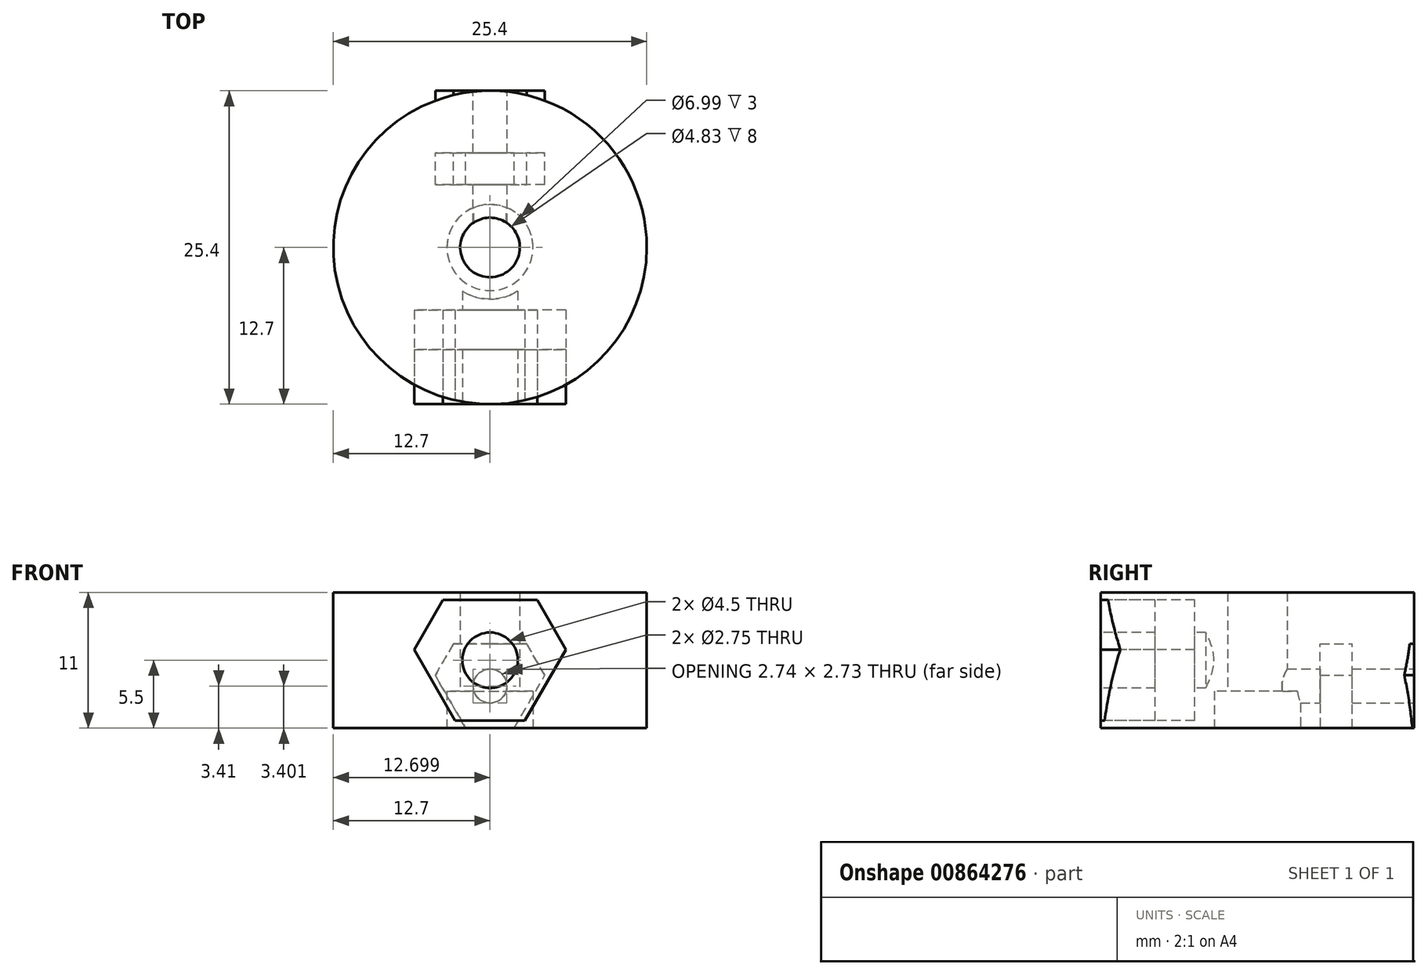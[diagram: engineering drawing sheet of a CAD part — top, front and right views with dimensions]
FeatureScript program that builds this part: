
annotation { "Feature Type Name" : "Feature", "Feature Type Description" : "" }
export const myFeature = defineFeature(function(context is Context, id is Id, definition is map)
    precondition{}
    {
        {
            var Q0;
            Q0=qCreatedBy(makeId("Top.planeOp"),FACE);
            var sketch = newSketch(context, id + "F0", { "sketchPlane" : qUnion([Q0])});
            skCircle(sketch, "E0", {"center": v(0, 0) * mm, "radius": 3.5 * mm});
            skCircle(sketch, "E1", {"center": v(0, 0) * mm, "radius": 12.7 * mm});
            skSolve(sketch);
        }
        {
            var Q0;
            Q0 = qSketchRegion(id + "F0", true);
            extrude(context, id + "F1", {"entities" : qUnion([Q0]), "endBound" : BoundingType.SYMMETRIC, "depth" : 11 * mm, "offsetDistance" : 25.4 * mm});
        }
        {
            var Q0;
            Q0=qCreatedBy(makeId("Front.planeOp"),FACE);
            cPlane(context, id + "F2", {"entities" : qUnion([Q0]), "cplaneType" : CPlaneType.OFFSET, "offset" : 12.7 * mm, "width" : 152.4 * mm, "height" : 152.4 * mm});
        }
        {
            var Q0;
            Q0=qCreatedBy(id+"F2.planeOp",FACE);
            var sketch = newSketch(context, id + "F3", { "sketchPlane" : qUnion([Q0])});
            skCircle(sketch, "E2", {"center": v(0, 0) * mm, "radius": 2.25 * mm});
            skSolve(sketch);
        }
        {
            var Q0;
            Q0=makeQuery(id+"F3.imprint","IMPRINT",FACE,{"disambiguationData":[TD([[makeQuery(id+"F3.imprint","IMPRINT",EDGE,{"derivedFrom":sQuery(id+"F3.wireOp",EDGE,"E2")}),1.0]])]});
            extrude(context, id + "F4", {"entities" : qUnion([Q0]), "operationType" : NewBodyOperationType.REMOVE, "oppositeDirection" : true, "depth" : 7.62 * mm, "offsetDistance" : 25.4 * mm});
        }
        {
            var Q0;
            Q0=qCreatedBy(id+"F2.planeOp",FACE);
            var sketch = newSketch(context, id + "F5", { "sketchPlane" : qUnion([Q0])});
            skCircle(sketch, "E3.cCircle", {"center": v(0, 0) * mm, "radius": 4.89 * mm, "construction": true});
            skLineSegment(sketch, "E3.0", {"start": v(2.82, -4.89) * mm, "end": v(-2.82, -4.89) * mm});
            skLineSegment(sketch, "E3.1", {"start": v(-2.82, -4.89) * mm, "end": v(-5.65, 0) * mm});
            skLineSegment(sketch, "E3.2", {"start": v(-5.65, 0) * mm, "end": v(-2.82, 4.89) * mm});
            skLineSegment(sketch, "E3.3", {"start": v(-2.82, 4.89) * mm, "end": v(2.82, 4.89) * mm});
            skLineSegment(sketch, "E3.4", {"start": v(2.82, 4.89) * mm, "end": v(5.65, 0) * mm});
            skLineSegment(sketch, "E3.5", {"start": v(5.65, 0) * mm, "end": v(2.82, -4.89) * mm});
            skPoint(sketch, "E3.0.midPoint", {"position": v(0, -4.89) * mm});
            skLineSegment(sketch, "E4", {"start": v(-5.65, 0) * mm, "end": v(-6.15, 0.87) * mm});
            skLineSegment(sketch, "E5", {"start": v(-6.15, 0.87) * mm, "end": v(-3.82, 4.89) * mm});
            skLineSegment(sketch, "E6", {"start": v(-3.82, 4.89) * mm, "end": v(-2.82, 4.89) * mm});
            skLineSegment(sketch, "E7.MirrorCS", {"start": v(5.65, 0) * mm, "end": v(6.15, 0.87) * mm});
            skLineSegment(sketch, "E8.MirrorCS", {"start": v(3.82, 4.89) * mm, "end": v(2.82, 4.89) * mm});
            skLineSegment(sketch, "E9.MirrorCS", {"start": v(6.15, 0.87) * mm, "end": v(3.82, 4.89) * mm});
            skSolve(sketch);
        }
        {
            var Q0;
            Q0=makeQuery(id+"F5.imprint","IMPRINT",FACE,{"disambiguationData":[TD([[makeQuery(id+"F5.imprint","IMPRINT",EDGE,{"derivedFrom":sQuery(id+"F5.wireOp",EDGE,"E3.2")}),1.0]])]});
            var Q1;
            Q1=makeQuery(id+"F5.imprint","IMPRINT",FACE,{"disambiguationData":[TD([[makeQuery(id+"F5.imprint","IMPRINT",EDGE,{"derivedFrom":sQuery(id+"F5.wireOp",EDGE,"E3.0")}),-1.0]])]});
            var Q2;
            Q2=makeQuery(id+"F5.imprint","IMPRINT",FACE,{"disambiguationData":[TD([[makeQuery(id+"F5.imprint","IMPRINT",EDGE,{"derivedFrom":sQuery(id+"F5.wireOp",EDGE,"E3.4")}),1.0]])]});
            extrude(context, id + "F6", {"entities" : qUnion([Q0, Q1, Q2]), "operationType" : NewBodyOperationType.REMOVE, "oppositeDirection" : true, "depth" : 7.62 * mm, "offsetDistance" : 25.4 * mm});
        }
        {
            var Q0;
            Q0 = qSketchRegion(id + "F5", true);
            extrude(context, id + "F7", {"entities" : qUnion([Q0]), "oppositeDirection" : true, "depth" : 7.62 * mm - 3.2 * mm, "offsetDistance" : 25.4 * mm});
        }
        {
            var Q0;
            Q0 = qSketchRegion(id + "F3", true);
            extrude(context, id + "F8", {"entities" : qUnion([Q0]), "operationType" : NewBodyOperationType.REMOVE, "oppositeDirection" : true, "depth" : 12.7 * mm, "offsetDistance" : 25.4 * mm});
        }
        {
            var Q0;
            Q0=qCreatedBy(makeId("Top.planeOp"),FACE);
            var sketch = newSketch(context, id + "F9", { "sketchPlane" : qUnion([Q0])});
            skCircle(sketch, "E10", {"center": v(0, 0) * mm, "radius": 2.41 * mm});
            skCircle(sketch, "E11", {"center": v(0, 0) * mm, "radius": 4.19 * mm});
            skSolve(sketch);
        }
        {
            var Q0;
            Q0=makeQuery(id+"F9.imprint","IMPRINT",FACE,{"disambiguationData":[TD([[makeQuery(id+"F9.imprint","IMPRINT",EDGE,{"derivedFrom":sQuery(id+"F9.wireOp",EDGE,"E10")}),-1.0]])]});
            extrude(context, id + "F10", {"entities" : qUnion([Q0]), "operationType" : NewBodyOperationType.ADD, "depth" : 5.5 * mm, "offsetDistance" : 25.4 * mm, "hasSecondDirection" : true, "secondDirectionOppositeDirection" : true, "secondDirectionDepth" : 2.5 * mm});
        }
        {
            var Q0;
            Q0=qCreatedBy(id+"F2.planeOp",FACE);
            cPlane(context, id + "F11", {"entities" : qUnion([Q0]), "cplaneType" : CPlaneType.OFFSET, "offset" : 25.4 * mm, "oppositeDirection" : true, "width" : 152.4 * mm, "height" : 152.4 * mm});
        }
        {
            var Q0;
            Q0=qCreatedBy(id+"F11.planeOp",FACE);
            var sketch = newSketch(context, id + "F12", { "sketchPlane" : qUnion([Q0])});
            skCircle(sketch, "E12.cCircle", {"center": v(0, -2.09) * mm, "radius": 3.41 * mm, "construction": true});
            skLineSegment(sketch, "E12.0", {"start": v(1.97, -5.5) * mm, "end": v(-1.97, -5.5) * mm});
            skLineSegment(sketch, "E12.1", {"start": v(-1.97, -5.5) * mm, "end": v(-3.94, -2.09) * mm});
            skLineSegment(sketch, "E12.2", {"start": v(-3.94, -2.09) * mm, "end": v(-1.97, 1.32) * mm});
            skLineSegment(sketch, "E12.3", {"start": v(-1.97, 1.32) * mm, "end": v(1.97, 1.32) * mm});
            skLineSegment(sketch, "E12.4", {"start": v(1.97, 1.32) * mm, "end": v(3.94, -2.09) * mm});
            skLineSegment(sketch, "E12.5", {"start": v(3.94, -2.09) * mm, "end": v(1.97, -5.5) * mm});
            skPoint(sketch, "E12.0.midPoint", {"position": v(0, -5.5) * mm});
            skLineSegment(sketch, "E13", {"start": v(3.94, -2.09) * mm, "end": v(4.44, -1.22) * mm});
            skLineSegment(sketch, "E14", {"start": v(4.44, -1.22) * mm, "end": v(2.97, 1.32) * mm});
            skLineSegment(sketch, "E15", {"start": v(2.97, 1.32) * mm, "end": v(1.97, 1.32) * mm});
            skLineSegment(sketch, "E16.MirrorCS", {"start": v(-3.94, -2.09) * mm, "end": v(-4.44, -1.22) * mm});
            skLineSegment(sketch, "E17.MirrorCS", {"start": v(-2.97, 1.32) * mm, "end": v(-1.97, 1.32) * mm});
            skLineSegment(sketch, "E18.MirrorCS", {"start": v(-4.44, -1.22) * mm, "end": v(-2.97, 1.32) * mm});
            skCircle(sketch, "E19", {"center": v(0, -2.09) * mm, "radius": 1.38 * mm});
            skSolve(sketch);
        }
        {
            var Q0;
            Q0=makeQuery(id+"F12.imprint","IMPRINT",FACE,{"disambiguationData":[TD([[makeQuery(id+"F12.imprint","IMPRINT",EDGE,{"derivedFrom":sQuery(id+"F12.wireOp",EDGE,"E12.2")}),1.0]])]});
            var Q1;
            Q1=makeQuery(id+"F12.imprint","IMPRINT",FACE,{"disambiguationData":[TD([[makeQuery(id+"F12.imprint","IMPRINT",EDGE,{"derivedFrom":sQuery(id+"F12.wireOp",EDGE,"E12.0")}),-1.0]])]});
            var Q2;
            Q2=makeQuery(id+"F12.imprint","IMPRINT",FACE,{"disambiguationData":[TD([[makeQuery(id+"F12.imprint","IMPRINT",EDGE,{"derivedFrom":sQuery(id+"F12.wireOp",EDGE,"E12.4")}),1.0]])]});
            extrude(context, id + "F13", {"entities" : qUnion([Q0, Q1, Q2]), "operationType" : NewBodyOperationType.REMOVE, "depth" : 7.62 * mm, "offsetDistance" : 25.4 * mm});
        }
        {
            var Q0;
            Q0 = qSketchRegion(id + "F12", true);
            extrude(context, id + "F14", {"entities" : qUnion([Q0]), "operationType" : NewBodyOperationType.ADD, "depth" : 7.62 * mm - (2.36 * 1.1) * mm, "offsetDistance" : 25.4 * mm});
        }
        {
            var Q0;
            Q0=makeQuery(id+"F14.opExtrude","CAP_FACE",FACE,{"disambiguationData":[OSD([sQuery(id+"F12.wireOp",EDGE,"E12.0"),sQuery(id+"F12.wireOp",EDGE,"E12.1"),sQuery(id+"F12.wireOp",EDGE,"E12.3"),sQuery(id+"F12.wireOp",EDGE,"E12.5"),sQuery(id+"F12.wireOp",EDGE,"E13"),sQuery(id+"F12.wireOp",EDGE,"E14"),sQuery(id+"F12.wireOp",EDGE,"E15"),sQuery(id+"F12.wireOp",EDGE,"E16.MirrorCS"),sQuery(id+"F12.wireOp",EDGE,"E17.MirrorCS"),sQuery(id+"F12.wireOp",EDGE,"E18.MirrorCS"),sQuery(id+"F12.wireOp",EDGE,"E19")])],"isStart":true});
            var sketch = newSketch(context, id + "F15", { "sketchPlane" : qUnion([Q0])});
            skCircle(sketch, "E20", {"center": v(0, -2.09) * mm, "radius": 1.37 * mm});
            skSolve(sketch);
        }
        {
            var Q0;
            Q0 = qSketchRegion(id + "F15", true);
            extrude(context, id + "F16", {"entities" : qUnion([Q0]), "operationType" : NewBodyOperationType.REMOVE, "oppositeDirection" : true, "depth" : 12.7 * mm, "offsetDistance" : 25.4 * mm});
        }
    });
